# Revit family: Accessory-Flush_Actuator_Plate-KOHLER-BEVEL-K-8857IN
name_source: partatom
category: Specialty Equipment
revit_build: Autodesk Revit 2017 (Build: 20160225_1515(x64)
units: mm (PartAtom-declared; Revit-internal decimal feet)

## family parameters
Cut with Voids When Loaded = No
Host = Face
OmniClass Number = 23.31.25.00
OmniClass Title = Toilet and Bath Specialties
Part Type = Normal
Room Calculation Point = No
Round Connector Dimension = Use Diameter
Shared = No

## types (3) — shared parameters
ADA Compliant = No
Assembly Code = C1030200
Date Modified = 01/05/2021
Default Elevation = 42"
Description = Faceplate For Instaflush Mechanical Tank
Height = 6 5/16"
Length = 1/2"
Manufacturer = KOHLER Co.
Master Format 2014 = 10 28 00
Master Format 2014 Name = Toilet, Bath, and Laundry Accessories
Material = Plastic
Product Documentation Link = http://resources.kohler.com
Product Name = BEVEL
Product Page URL = https://www.kohler.co.in
URL = https://www.kohler.co.in
WaterSense Certified = No
Width = 8 7/8"

## per-type parameters (varying)
| type | Finish | Model | Type |
| CP- Polished Chrome | KOHLER-Plastic-CP-Polished_Chrome | K-8857IN-M-CP | 1 |
| MS1-Satin Chrome | Kohler-Plastic-MS1-Satin_Chrome | K-8857IN-M-MS1 | 2 |
| AF-French Gold | KOHLER-Plastic-AF-Vibrant_French_Gold | K-8857IN-M-AF | 3 |

## geometry (parser evidence)
native form markers: Sweep x5
no freeform markers — native parametric forms only
